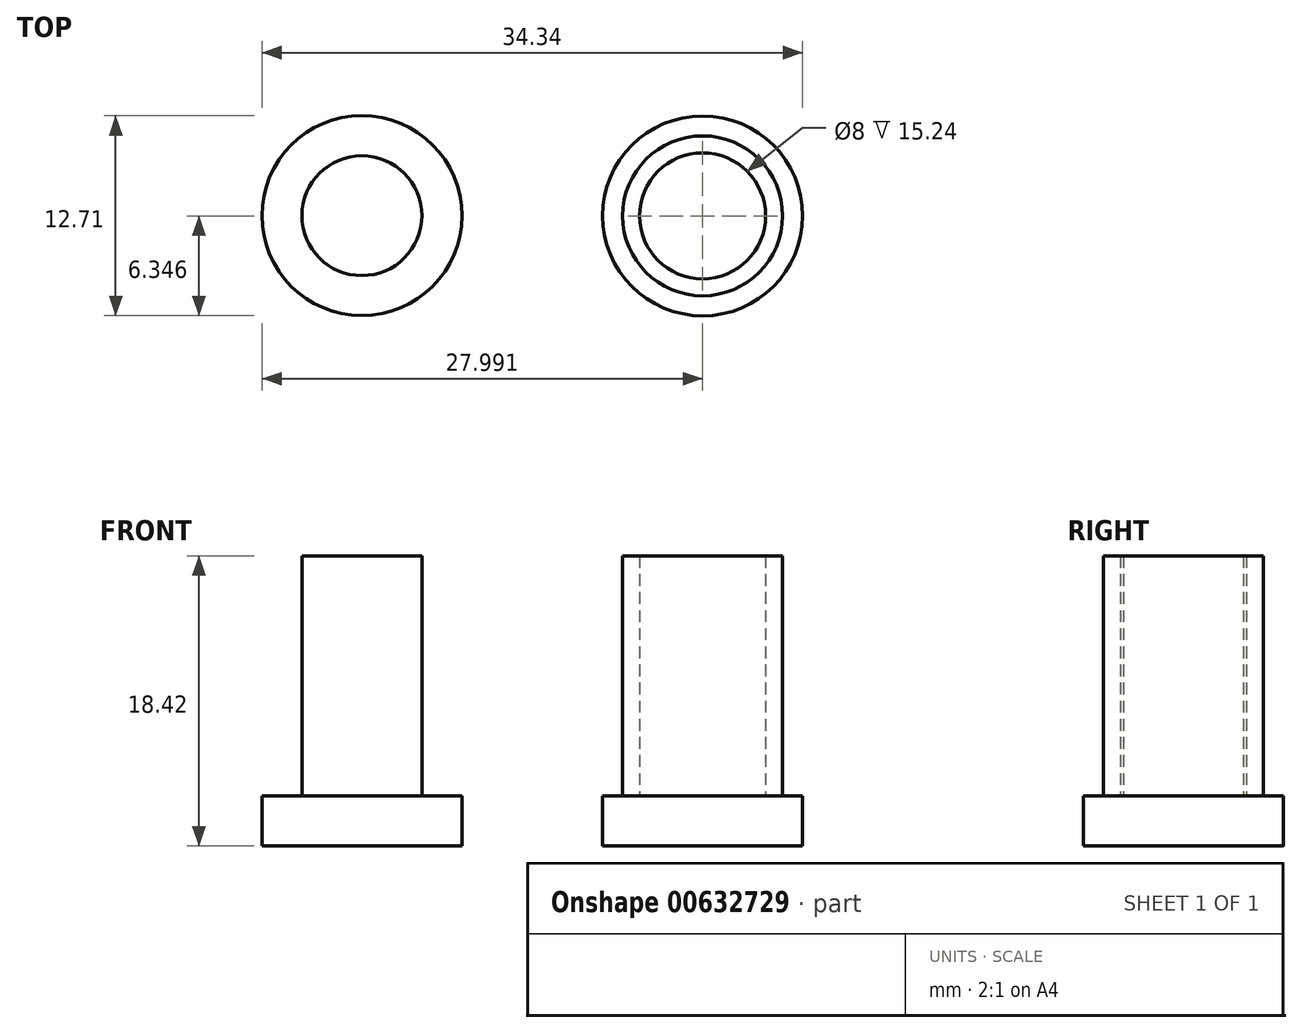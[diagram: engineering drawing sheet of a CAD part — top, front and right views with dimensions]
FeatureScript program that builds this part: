
annotation { "Feature Type Name" : "Feature", "Feature Type Description" : "" }
export const myFeature = defineFeature(function(context is Context, id is Id, definition is map)
    precondition{}
    {
        {
            var Q0;
            Q0=qCreatedBy(makeId("Top.planeOp"),FACE);
            var sketch = newSketch(context, id + "F0", { "sketchPlane" : qUnion([Q0])});
            skCircle(sketch, "E0", {"center": v(0, 0) * mm, "radius": 6.35 * mm});
            skSolve(sketch);
        }
        {
            var Q0;
            Q0=makeQuery(id+"F0.imprint","IMPRINT",FACE,{"disambiguationData":[TD([[makeQuery(id+"F0.imprint","IMPRINT",EDGE,{"derivedFrom":sQuery(id+"F0.wireOp",EDGE,"E0")}),1.0]])]});
            extrude(context, id + "F1", {"entities" : qUnion([Q0]), "depth" : 3.17 * mm, "offsetDistance" : 25.4 * mm});
        }
        {
            var Q0;
            Q0=makeQuery(id+"F1.opExtrude","CAP_FACE",FACE,{"disambiguationData":[OSD([sQuery(id+"F0.wireOp",EDGE,"E0")])],"isStart":false});
            var sketch = newSketch(context, id + "F2", { "sketchPlane" : qUnion([Q0])});
            skCircle(sketch, "E1", {"center": v(0, 0) * mm, "radius": 3.81 * mm});
            skSolve(sketch);
        }
        {
            var Q0;
            Q0=makeQuery(id+"F2.imprint","IMPRINT",FACE,{"disambiguationData":[TD([[makeQuery(id+"F2.imprint","IMPRINT",EDGE,{"derivedFrom":sQuery(id+"F2.wireOp",EDGE,"E1")}),1.0]])]});
            extrude(context, id + "F3", {"entities" : qUnion([Q0]), "operationType" : NewBodyOperationType.ADD, "depth" : 15.24 * mm, "offsetDistance" : 25.4 * mm});
        }
        {
            var Q0;
            Q0=qCreatedBy(makeId("Top.planeOp"),FACE);
            var sketch = newSketch(context, id + "F4", { "sketchPlane" : qUnion([Q0])});
            skCircle(sketch, "E2", {"center": v(21.64, -0.01) * mm, "radius": 6.35 * mm});
            skSolve(sketch);
        }
        {
            var Q0;
            Q0=makeQuery(id+"F4.imprint","IMPRINT",FACE,{"disambiguationData":[TD([[makeQuery(id+"F4.imprint","IMPRINT",EDGE,{"derivedFrom":sQuery(id+"F4.wireOp",EDGE,"E2")}),1.0]])]});
            extrude(context, id + "F5", {"entities" : qUnion([Q0]), "depth" : 3.17 * mm, "offsetDistance" : 25.4 * mm});
        }
        {
            var Q0;
            Q0=makeQuery(id+"F5.opExtrude","CAP_FACE",FACE,{"disambiguationData":[OSD([sQuery(id+"F4.wireOp",EDGE,"E2")])],"isStart":false});
            var sketch = newSketch(context, id + "F6", { "sketchPlane" : qUnion([Q0])});
            skCircle(sketch, "E3", {"center": v(21.64, -0.01) * mm, "radius": 4 * mm});
            skCircle(sketch, "E4", {"center": v(21.64, -0.01) * mm, "radius": 5.08 * mm});
            skSolve(sketch);
        }
        {
            var Q0;
            Q0=makeQuery(id+"F6.imprint","IMPRINT",FACE,{"disambiguationData":[TD([[makeQuery(id+"F6.imprint","IMPRINT",EDGE,{"derivedFrom":sQuery(id+"F6.wireOp",EDGE,"E3")}),-1.0]])]});
            extrude(context, id + "F7", {"entities" : qUnion([Q0]), "operationType" : NewBodyOperationType.ADD, "depth" : 15.24 * mm, "offsetDistance" : 25.4 * mm});
        }
    });
